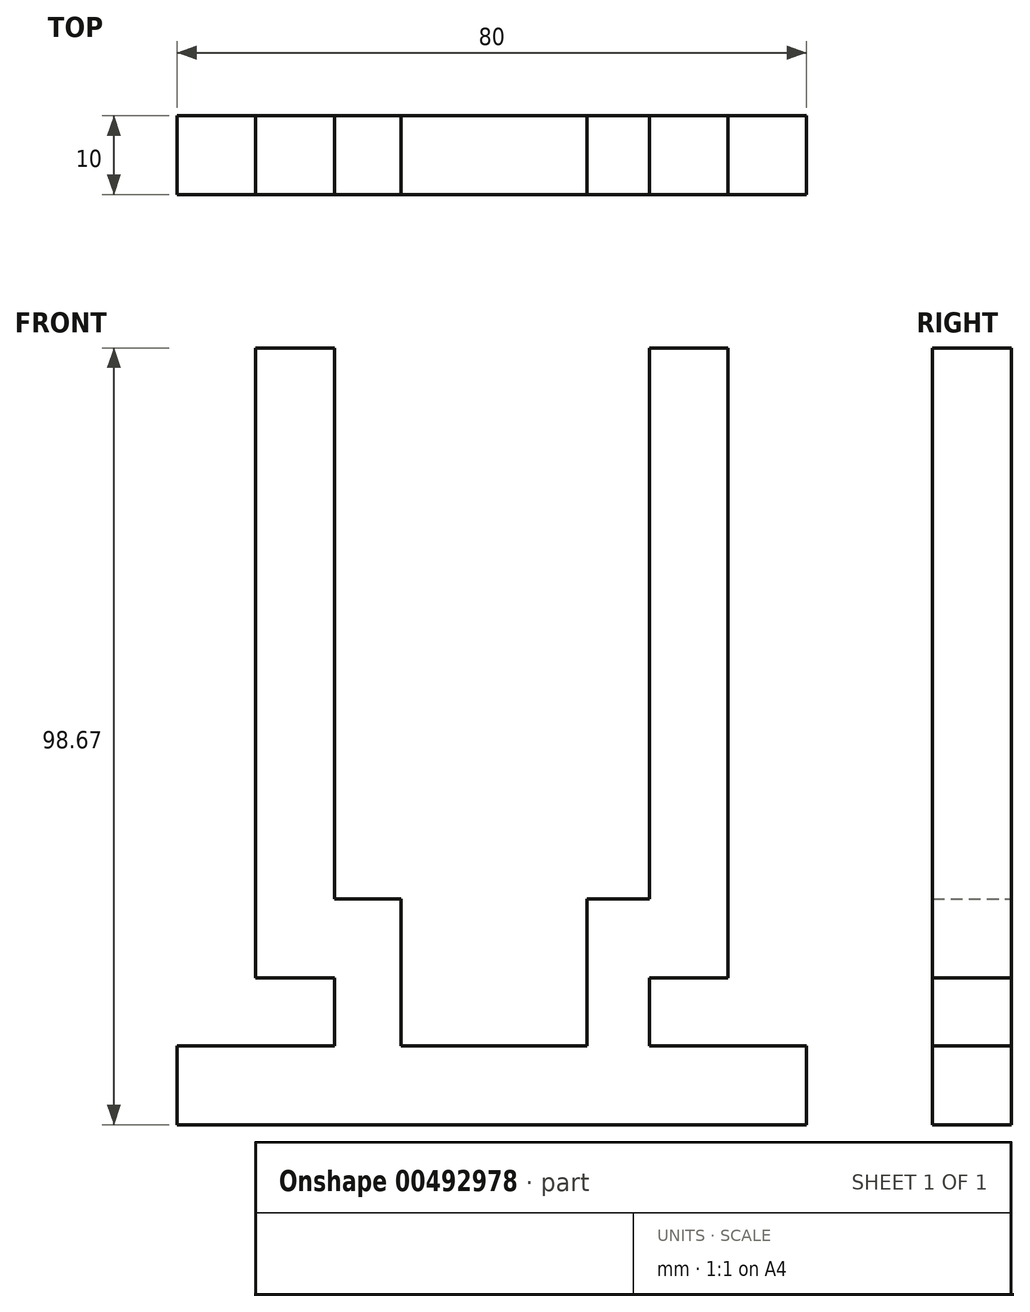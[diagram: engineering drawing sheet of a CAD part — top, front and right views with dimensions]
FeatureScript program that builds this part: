
annotation { "Feature Type Name" : "Feature", "Feature Type Description" : "" }
export const myFeature = defineFeature(function(context is Context, id is Id, definition is map)
    precondition{}
    {
        {
            var Q0;
            Q0=qCreatedBy(makeId("Front.planeOp"),FACE);
            var sketch = newSketch(context, id + "F0", { "sketchPlane" : qUnion([Q0])});
            skLineSegment(sketch, "E0", {"start": v(-17.29, 0) * mm, "end": v(62.71, 0) * mm});
            skLineSegment(sketch, "E1", {"start": v(62.71, 0) * mm, "end": v(62.71, 10) * mm});
            skLineSegment(sketch, "E2", {"start": v(-17.29, 10) * mm, "end": v(-17.29, 0) * mm});
            skLineSegment(sketch, "E3", {"start": v(-17.29, 10) * mm, "end": v(62.71, 10) * mm});
            skLineSegment(sketch, "E4.bottom", {"start": v(-7.29, 18.67) * mm, "end": v(2.71, 18.67) * mm});
            skLineSegment(sketch, "E4.top", {"start": v(-7.29, 98.67) * mm, "end": v(2.71, 98.67) * mm});
            skLineSegment(sketch, "E4.left", {"start": v(-7.29, 18.67) * mm, "end": v(-7.29, 98.67) * mm});
            skLineSegment(sketch, "E4.right", {"start": v(2.71, 18.67) * mm, "end": v(2.71, 98.67) * mm});
            skLineSegment(sketch, "E5.bottom", {"start": v(42.71, 98.67) * mm, "end": v(52.71, 98.67) * mm});
            skLineSegment(sketch, "E5.top", {"start": v(42.71, 18.67) * mm, "end": v(52.71, 18.67) * mm});
            skLineSegment(sketch, "E5.left", {"start": v(42.71, 98.67) * mm, "end": v(42.71, 18.67) * mm});
            skLineSegment(sketch, "E5.right", {"start": v(52.71, 98.67) * mm, "end": v(52.71, 18.67) * mm});
            skLineSegment(sketch, "E6.bottom", {"start": v(2.71, 10) * mm, "end": v(11.18, 10) * mm});
            skLineSegment(sketch, "E6.top", {"start": v(2.71, 28.67) * mm, "end": v(11.18, 28.67) * mm});
            skLineSegment(sketch, "E6.left", {"start": v(2.71, 10) * mm, "end": v(2.71, 28.67) * mm});
            skLineSegment(sketch, "E6.right", {"start": v(11.18, 10) * mm, "end": v(11.18, 28.67) * mm});
            skLineSegment(sketch, "E7.bottom", {"start": v(42.71, 10) * mm, "end": v(34.83, 10) * mm});
            skLineSegment(sketch, "E7.top", {"start": v(42.71, 28.67) * mm, "end": v(34.83, 28.67) * mm});
            skLineSegment(sketch, "E7.left", {"start": v(42.71, 10) * mm, "end": v(42.71, 28.67) * mm});
            skLineSegment(sketch, "E7.right", {"start": v(34.83, 10) * mm, "end": v(34.83, 28.67) * mm});
            skSolve(sketch);
        }
        {
            var Q0;
            Q0 = qSketchRegion(id + "F0", true);
            extrude(context, id + "F1", {"entities" : qUnion([Q0]), "depth" : 10 * mm});
        }
    });
